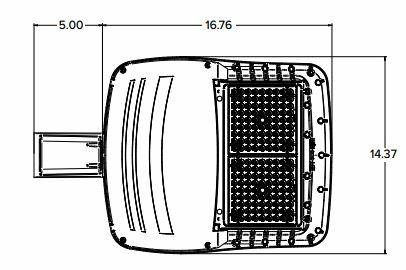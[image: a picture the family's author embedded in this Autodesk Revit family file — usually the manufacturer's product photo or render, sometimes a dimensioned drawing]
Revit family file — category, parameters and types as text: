
# Revit family: VP-3-T
name_source: partatom
category: Lighting Fixtures
units: mm (PartAtom-declared; Revit-internal decimal feet)

## family parameters
Cut with Voids When Loaded = No
Host = Face
Light Source = No
OmniClass Number = 23.80.70.11.14.17
OmniClass Title = Direct/Indirect
Part Type = Normal
Room Calculation Point = No
Round Connector Dimension = Use Diameter
Shared = Yes

## types (1)
- VP-3-T
    Apparent Load = 423 VA
    Assembly Code = D5020200
    Brand = Beacon
    CRI = 70
    Certification = UL
    Cool Grey = Cool Grey
    Default Elevation = 48 "
    Description = The Viper is an extremely versatile area/site luminaire which blends design, performance, and technology for a variety of applications.
    Features = Featuring two different optical technologies, Micro Strike and Strike Optics, which provide the best distribution patterns for retrofit or new construction
Vibration rated for high vibration applications including bridges and overpasses
Control options including photo control, occupancy sensing, NX Lighting Controls, wiSCAPE and 7-Pin with networked controls
Mounting options include: Arm, Universal Arm, Adjustable Arm, Mast Arm, Decorative Arm, Knuckle, Trunnion, Wall
Distribution options include: Auto Front Row, Type 2, Type 3, Type 4 Forward, Type 4 Wide, Type 5 Narrow, Type 5 Medium, Type 5 Wide, Type 5 Rectangular, Corner Optic, and Tennis Court
    Finish = Arctic White
    Glass = Glass
    Grey = Grey
    Lamp = LED
    Light Output = 30846 cd/m²
    Load Classification = Lighting
    Manufacturer = Current Lighting
    Matt Black = Matt Black
    Matt Grey = MATT GREY
    Matt White = Matt White
    Model = VP-3-T
    Name = Viper Area Size 3
    Power Factor = 0.9
    Product Documentation Link = https://cdn.currentlighting.com
    Product Page URL = https://www.currentlighting.com
    Type Comments = Lighting Fixture
    URL = https://www.currentlighting.com
    Voltage = 120 V
    Warranty = Five year warranty
    Wattage Comments = 423W

## geometry (parser evidence)
native form markers: Blend x4, Sweep x4
no freeform markers — native parametric forms only
